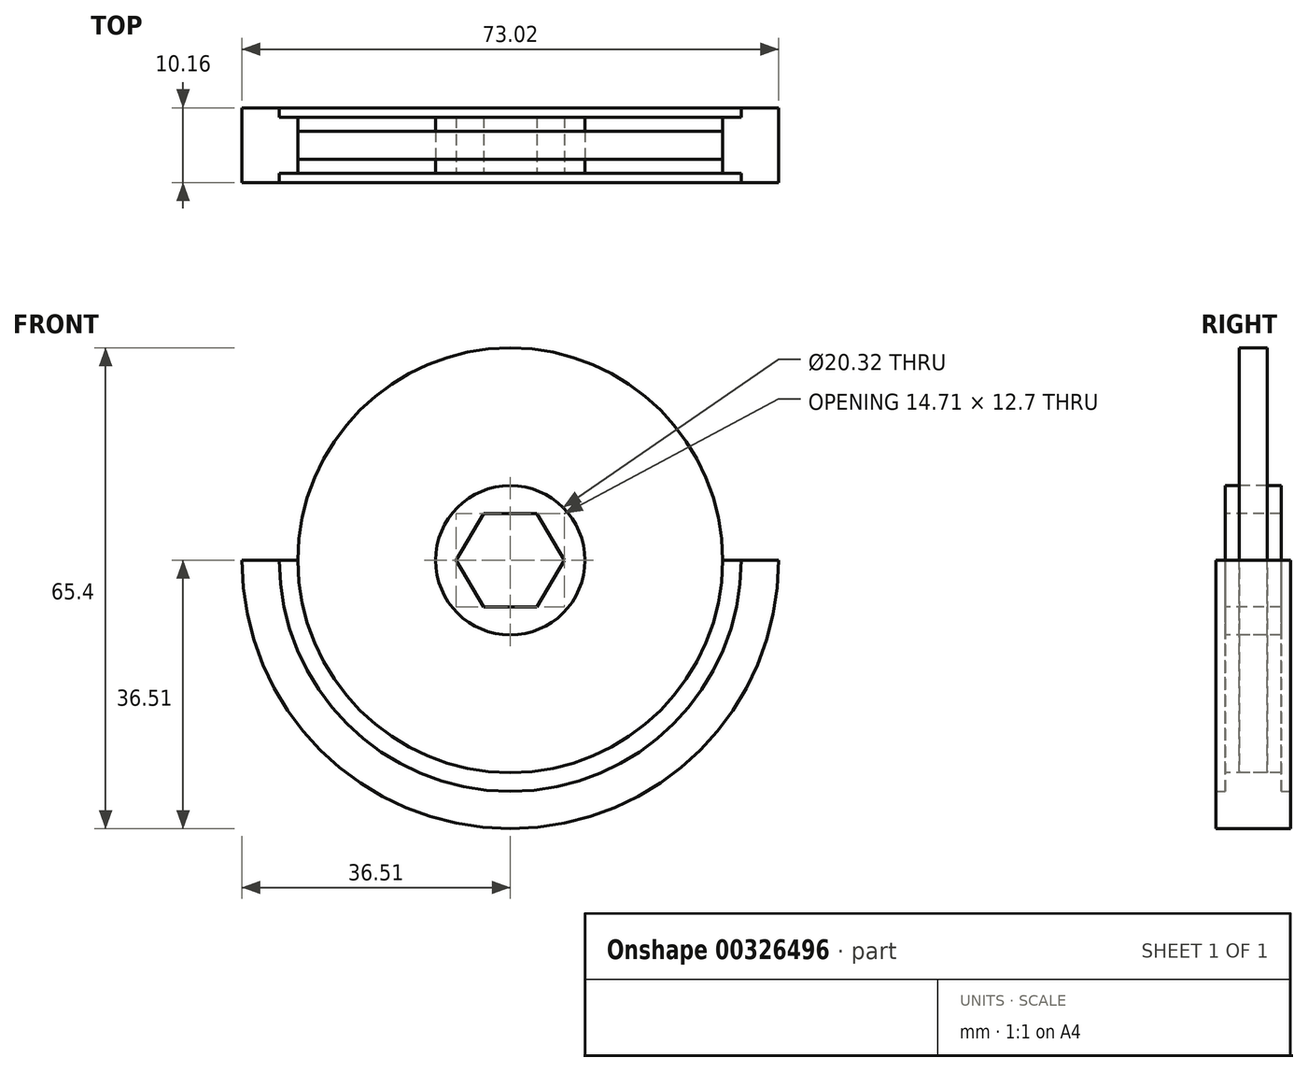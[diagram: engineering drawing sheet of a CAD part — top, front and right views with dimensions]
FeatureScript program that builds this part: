
annotation { "Feature Type Name" : "Feature", "Feature Type Description" : "" }
export const myFeature = defineFeature(function(context is Context, id is Id, definition is map)
    precondition{}
    {
        {
            var Q0;
            Q0=qCreatedBy(makeId("Front.planeOp"),FACE);
            var sketch = newSketch(context, id + "F0", { "sketchPlane" : qUnion([Q0])});
            skCircle(sketch, "E0", {"center": v(0, 0) * mm, "radius": 31.43 * mm});
            skCircle(sketch, "E1", {"center": v(0, 0) * mm, "radius": 36.51 * mm});
            skLineSegment(sketch, "E2", {"start": v(0, 54.83) * mm, "end": v(0, -52.62) * mm});
            skLineSegment(sketch, "E3", {"start": v(-43.96, 0) * mm, "end": v(47.64, 0) * mm});
            skLineSegment(sketch, "E4", {"start": v(0, 6.35) * mm, "end": v(-3.64, 6.35) * mm});
            skLineSegment(sketch, "E5", {"start": v(-3.64, 6.35) * mm, "end": v(-7.35, 0) * mm});
            skCircle(sketch, "E6", {"center": v(0, 0) * mm, "radius": 28.9 * mm});
            skLineSegment(sketch, "E7.MirrorCS", {"start": v(0, -6.35) * mm, "end": v(-3.64, -6.35) * mm});
            skLineSegment(sketch, "E8.MirrorCS", {"start": v(-3.64, -6.35) * mm, "end": v(-7.35, 0) * mm});
            skLineSegment(sketch, "E9.MirrorCS", {"start": v(3.64, -6.35) * mm, "end": v(7.35, 0) * mm});
            skLineSegment(sketch, "E10.MirrorCS", {"start": v(3.64, 6.35) * mm, "end": v(7.35, 0) * mm});
            skLineSegment(sketch, "E11.MirrorCS", {"start": v(0, -6.35) * mm, "end": v(3.64, -6.35) * mm});
            skLineSegment(sketch, "E12.MirrorCS", {"start": v(0, 6.35) * mm, "end": v(3.64, 6.35) * mm});
            skCircle(sketch, "E13", {"center": v(0, 0) * mm, "radius": 10.16 * mm});
            skSolve(sketch);
        }
        {
            var Q0;
            {var subQ0=sQuery(id+"F0.wireOp",EDGE,"E2");var subQ1=sQuery(id+"F0.wireOp",EDGE,"E0");var subQ2=makeQuery(id+"F0.imprint","INTERSECT",VERTEX,{"disambiguationData":[OD(0.0)],"derivedFrom":[subQ1,subQ0]});Q0=makeQuery(id+"F0.imprint","IMPRINT",FACE,{"disambiguationData":[TD([[makeQuery(id+"F0.imprint","IMPRINT",EDGE,{"disambiguationData":[TD([[subQ2,1.0]])],"derivedFrom":subQ1}),-1.0]])]});}
            var Q1;
            {var subQ0=sQuery(id+"F0.wireOp",EDGE,"E3");var subQ1=sQuery(id+"F0.wireOp",EDGE,"E0");var subQ2=makeQuery(id+"F0.imprint","INTERSECT",VERTEX,{"disambiguationData":[OD(1.0)],"derivedFrom":[subQ1,subQ0]});Q1=makeQuery(id+"F0.imprint","IMPRINT",FACE,{"disambiguationData":[TD([[makeQuery(id+"F0.imprint","IMPRINT",EDGE,{"disambiguationData":[TD([[subQ2,-1.0]])],"derivedFrom":subQ1}),-1.0]])]});}
            var Q2;
            {var subQ0=sQuery(id+"F0.wireOp",EDGE,"E3");var subQ1=sQuery(id+"F0.wireOp",EDGE,"E0");var subQ2=makeQuery(id+"F0.imprint","INTERSECT",VERTEX,{"disambiguationData":[OD(0.0)],"derivedFrom":[subQ1,subQ0]});Q2=makeQuery(id+"F0.imprint","IMPRINT",FACE,{"disambiguationData":[TD([[makeQuery(id+"F0.imprint","IMPRINT",EDGE,{"disambiguationData":[TD([[subQ2,1.0]])],"derivedFrom":subQ1}),-1.0]])]});}
            var Q3;
            {var subQ0=sQuery(id+"F0.wireOp",EDGE,"E2");var subQ1=sQuery(id+"F0.wireOp",EDGE,"E0");var subQ2=makeQuery(id+"F0.imprint","INTERSECT",VERTEX,{"disambiguationData":[OD(0.0)],"derivedFrom":[subQ1,subQ0]});Q3=makeQuery(id+"F0.imprint","IMPRINT",FACE,{"disambiguationData":[TD([[makeQuery(id+"F0.imprint","IMPRINT",EDGE,{"disambiguationData":[TD([[subQ2,-1.0]])],"derivedFrom":subQ1}),-1.0]])]});}
            extrude(context, id + "F1", {"entities" : qUnion([Q0, Q1, Q2, Q3]), "endBound" : BoundingType.SYMMETRIC, "depth" : 10.16 * mm});
        }
        {
            var Q0;
            {var subQ1=sQuery(id+"F0.wireOp",EDGE,"E4");Q0=makeQuery(id+"F0.imprint","IMPRINT",FACE,{"disambiguationData":[TD([[makeQuery(id+"F0.imprint","IMPRINT",EDGE,{"derivedFrom":subQ1}),-1.0]])]});}
            var Q1;
            {var subQ0=sQuery(id+"F0.wireOp",EDGE,"E10.MirrorCS");Q1=makeQuery(id+"F0.imprint","IMPRINT",FACE,{"disambiguationData":[TD([[makeQuery(id+"F0.imprint","IMPRINT",EDGE,{"derivedFrom":subQ0}),1.0]])]});}
            var Q2;
            {var subQ1=sQuery(id+"F0.wireOp",EDGE,"E9.MirrorCS");Q2=makeQuery(id+"F0.imprint","IMPRINT",FACE,{"disambiguationData":[TD([[makeQuery(id+"F0.imprint","IMPRINT",EDGE,{"derivedFrom":subQ1}),-1.0]])]});}
            var Q3;
            {var subQ4=sQuery(id+"F0.wireOp",EDGE,"E7.MirrorCS");Q3=makeQuery(id+"F0.imprint","IMPRINT",FACE,{"disambiguationData":[TD([[makeQuery(id+"F0.imprint","IMPRINT",EDGE,{"derivedFrom":subQ4}),1.0]])]});}
            var Q4;
            {var subQ0=sQuery(id+"F0.wireOp",EDGE,"E2");var subQ1=sQuery(id+"F0.wireOp",EDGE,"E0");var subQ2=makeQuery(id+"F0.imprint","INTERSECT",VERTEX,{"disambiguationData":[OD(0.0)],"derivedFrom":[subQ1,subQ0]});Q4=makeQuery(id+"F0.imprint","IMPRINT",FACE,{"disambiguationData":[TD([[makeQuery(id+"F0.imprint","IMPRINT",EDGE,{"disambiguationData":[TD([[subQ2,-1.0]])],"derivedFrom":subQ1}),1.0]])]});}
            var Q5;
            {var subQ0=sQuery(id+"F0.wireOp",EDGE,"E2");var subQ1=sQuery(id+"F0.wireOp",EDGE,"E0");var subQ2=makeQuery(id+"F0.imprint","INTERSECT",VERTEX,{"disambiguationData":[OD(0.0)],"derivedFrom":[subQ1,subQ0]});Q5=makeQuery(id+"F0.imprint","IMPRINT",FACE,{"disambiguationData":[TD([[makeQuery(id+"F0.imprint","IMPRINT",EDGE,{"disambiguationData":[TD([[subQ2,1.0]])],"derivedFrom":subQ1}),1.0]])]});}
            var Q6;
            {var subQ0=sQuery(id+"F0.wireOp",EDGE,"E3");var subQ1=sQuery(id+"F0.wireOp",EDGE,"E0");var subQ2=makeQuery(id+"F0.imprint","INTERSECT",VERTEX,{"disambiguationData":[OD(0.0)],"derivedFrom":[subQ1,subQ0]});Q6=makeQuery(id+"F0.imprint","IMPRINT",FACE,{"disambiguationData":[TD([[makeQuery(id+"F0.imprint","IMPRINT",EDGE,{"disambiguationData":[TD([[subQ2,1.0]])],"derivedFrom":subQ1}),1.0]])]});}
            var Q7;
            {var subQ0=sQuery(id+"F0.wireOp",EDGE,"E3");var subQ1=sQuery(id+"F0.wireOp",EDGE,"E0");var subQ2=makeQuery(id+"F0.imprint","INTERSECT",VERTEX,{"disambiguationData":[OD(1.0)],"derivedFrom":[subQ1,subQ0]});Q7=makeQuery(id+"F0.imprint","IMPRINT",FACE,{"disambiguationData":[TD([[makeQuery(id+"F0.imprint","IMPRINT",EDGE,{"disambiguationData":[TD([[subQ2,-1.0]])],"derivedFrom":subQ1}),1.0]])]});}
            extrude(context, id + "F2", {"entities" : qUnion([Q0, Q1, Q2, Q3, Q4, Q5, Q6, Q7]), "operationType" : NewBodyOperationType.ADD, "endBound" : BoundingType.SYMMETRIC, "oppositeDirection" : true, "depth" : 7.62 * mm});
        }
        {
            var Q0;
            {var subQ0=sQuery(id+"F0.wireOp",EDGE,"E6");var subQ1=sQuery(id+"F0.wireOp",EDGE,"E2");var subQ2=makeQuery(id+"F0.imprint","INTERSECT",VERTEX,{"disambiguationData":[OD(0.0)],"derivedFrom":[subQ1,subQ0]});Q0=makeQuery(id+"F0.imprint","IMPRINT",FACE,{"disambiguationData":[TD([[makeQuery(id+"F0.imprint","IMPRINT",EDGE,{"disambiguationData":[TD([[subQ2,-1.0]])],"derivedFrom":subQ1}),1.0]])]});}
            var Q1;
            {var subQ0=sQuery(id+"F0.wireOp",EDGE,"E13");var subQ1=sQuery(id+"F0.wireOp",EDGE,"E2");var subQ2=makeQuery(id+"F0.imprint","INTERSECT",VERTEX,{"disambiguationData":[OD(1.0)],"derivedFrom":[subQ1,subQ0]});Q1=makeQuery(id+"F0.imprint","IMPRINT",FACE,{"disambiguationData":[TD([[makeQuery(id+"F0.imprint","IMPRINT",EDGE,{"disambiguationData":[TD([[subQ2,-1.0]])],"derivedFrom":subQ1}),1.0]])]});}
            var Q2;
            {var subQ0=sQuery(id+"F0.wireOp",EDGE,"E13");var subQ1=sQuery(id+"F0.wireOp",EDGE,"E2");var subQ2=makeQuery(id+"F0.imprint","INTERSECT",VERTEX,{"disambiguationData":[OD(1.0)],"derivedFrom":[subQ1,subQ0]});Q2=makeQuery(id+"F0.imprint","IMPRINT",FACE,{"disambiguationData":[TD([[makeQuery(id+"F0.imprint","IMPRINT",EDGE,{"disambiguationData":[TD([[subQ2,-1.0]])],"derivedFrom":subQ1}),-1.0]])]});}
            var Q3;
            {var subQ0=sQuery(id+"F0.wireOp",EDGE,"E6");var subQ1=sQuery(id+"F0.wireOp",EDGE,"E2");var subQ2=makeQuery(id+"F0.imprint","INTERSECT",VERTEX,{"disambiguationData":[OD(0.0)],"derivedFrom":[subQ1,subQ0]});Q3=makeQuery(id+"F0.imprint","IMPRINT",FACE,{"disambiguationData":[TD([[makeQuery(id+"F0.imprint","IMPRINT",EDGE,{"disambiguationData":[TD([[subQ2,-1.0]])],"derivedFrom":subQ1}),-1.0]])]});}
            extrude(context, id + "F3", {"entities" : qUnion([Q0, Q1, Q2, Q3]), "endBound" : BoundingType.SYMMETRIC, "oppositeDirection" : true, "depth" : 3.8 * mm});
        }
    });
